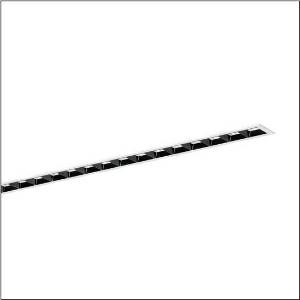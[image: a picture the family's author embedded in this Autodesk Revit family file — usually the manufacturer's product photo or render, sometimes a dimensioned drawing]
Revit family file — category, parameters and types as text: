
# Revit family: silica_r__21_51mx11tbt5w_4029
name_source: partatom
category: Lighting Fixtures
units: mm (PartAtom-declared; Revit-internal decimal feet)

## family parameters
Cut with Voids When Loaded = No
Host = Face
Light Source = No
Part Type = Normal
Room Calculation Point = No
Round Connector Dimension = Use Diameter
Shared = No

## types (1)
- --- (1 x LED, 4650 lm, 40.3 W, 6500K)
    Apparent Load = 40 VA
    CIE Flux Codes = 85 99 100 100 100
    Color Rendering = 80
    Color Temperature = 6500K
    Default Elevation = 1800 mm
    Description = Silica® 21, office luminaire, primary light control with darklight reflector, of PMMA, black, CAT 2 (L<= 3000cd/m²), light emission: direct distribution, primary light characteristic: symmetric, installation type: recessed, LED, rated luminous flux: 4.650lm, luminous efficacy: 110lm/W, light colour: 8tw, colour temperature: 2700..6500K, with terminal, 3+2-pole, max. 2.5mm², mains connection: 220..240V, AC, 50/60Hz, rated input power: 42.3W, luminaire housing, of aluminium, traffic white (RAL 9016), length: 1.528mm, width: 79mm, height: 53mm, protection rating (complete): IP20, insulation class (complete): insulation class I (protective earthing), certification: CE, permissible operating ambient temperature: 0..+35°C, standard: EN 50419, packaging unit: 1 piece
    Height = 0 mm  [stored 0 ft]
    Lamp = 1 x LED
    Lamp Light Flux = 4650 lm
    Lamp Power = 40.3 W
    Lamp count = 1
    Length = 1527 mm
    Luminous efficacy = 115 lm/W
    Manufacturer = Siteco
    ModVariant = No
    Model = 51MX11TBT5W
    Mounting Place = Ceiling
    Mounting Type = Recessed
    Number of Poles = 1
    OnlyDefault = Yes
    Power Factor = 1
    Product Name = Silica® 21
    Product group = office luminaire | ceiling recessed
    ProductGroupID = 400
    Protection Class = Protection class I
    Protection Degree = IP 20
    RLX_Detail_Level = 1
    RlxData = <blob elided: 39021 chars, md5=4bbe0cb7>
    Socket = socket
    Standby Power = 0 W
    System Light Flux = 4650 lm
    System Power = 40 W
    Type Comments = individual setting
    Type Image = l_1251632.jpg
    URL = http://relux.com
    VarID = @adj_046191
    Voltage = 0 V
    Weight = 0.00 kg
    Width = 79 mm

note: [stored X ft] marks values corroborated as IEEE doubles in the binary element streams (Revit-internal decimal feet)

## geometry (parser evidence)
native form markers: Blend x4, Sweep x9
no freeform markers — native parametric forms only
